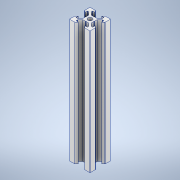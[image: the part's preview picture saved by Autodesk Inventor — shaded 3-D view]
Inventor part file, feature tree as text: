
AUTODESK INVENTOR PART (.ipt)
format: ipt  version: 2021 (Build 250183000, 183)  size: 238,080 bytes
history: native  units: mm
features: sketch x3, extrude x2, fillet x2, other x1, pattern_circular x1, hole x1, projected_geometry x1
ambient origin geometry x8: Origin, YZ Plane, XZ Plane, XY Plane, X Axis, Y Axis, Z Axis, Center Point
bodies: Body1 (feature_tree)
feature tree (11):
  other  "實體1"
  extrude  "擠出1"  Depth=20.0mm
  extrude  "擠出2"  Depth=20.0mm
  fillet  "圓角1"  Radius=120.0mm
  pattern_circular  "環形陣列1"  [2 undecoded]
  hole  "孔1"  [1 undecoded]
  fillet  "圓角2"  Radius=6.2mm
  sketch  "草圖1"
  sketch  "草圖2"
  projected_geometry  "投影迴路1"
  sketch  "草圖3"
note: 3 required parameter values undecoded (feature->parameter linkage not recoverable at this tier; creation-order binding heuristic only, values carry confidence <= 0.55)
